# Revit family: НЕВАТОМ_Стакaн монтажный SMK_20240620
name_source: partatom
category: Арматура воздуховодов
units: mm (PartAtom-declared; Revit-internal decimal feet)

## family parameters
Всегда вертикально = Да
На основе рабочей плоскости = Нет
Общий = Нет
При загрузке вырезать с полостями = Нет
Размер круглого соединителя = Использовать диаметр
Тип детали = Присоединяется

## types (12) — shared parameters
ADSK_Единица измерения = шт.
ADSK_Завод-изготовитель = НЕВАТОМ
ADSK_Количество = 1
ADSK_Материал наименование = Оцинкованная сталь
ADSK_Наименование = Стакан монтажный
Nevatom_URL = https://t.me
Ключевая пометка = Вентиляция
Материал = Оцинкованная сталь

## per-type parameters (varying)
| type | A | ADSK_Марка | ADSK_Масса | ADSK_Масса_Текст | ADSK_Размер_Высота | ADSK_Размер_Длина | ADSK_Размер_Ширина | B | D | H | L | L1 | L2 | НЕВАТОМ_Исполнение по комплектующим | НЕВАТОМ_Исполнение по конструкции | НЕВАТОМ_Материал_Нержавеющая сталь | НЕВАТОМ_Материал_Оцинкованная сталь | Сравнение материалов |
| SMK-031 | 400 мм | SMK-031-023-0-0 | 40 | 40.0 кг | 649 мм | 800 мм | 800 мм | 800 мм | 315 мм | 649 мм | 440 мм | 500 мм | 602 мм | 3 мм | 2 мм | Нет | Да | 0 мм |
| SMK-125 | 1435 мм | SMK-125-020-0-0 | 136 | 136.0 кг | 676 мм | 1845 мм | 1845 мм | 1845 мм | 1250 мм | 676 мм | 1550 мм | 1535 мм | 1698 мм | 0 мм | 2 мм | Нет | Да | 0 мм |
| SMK-040 | 470 мм | SMK-040-000-0-0 | 43 | 43.0 кг | 649 мм | 868 мм | 868 мм | 868 мм | 400 мм | 649 мм | 530 мм | 570 мм | 675 мм | 0 мм | 0 мм | Нет | Да | 0 мм |
| SMK-050 | 590 мм | SMK-050-000-0-0 | 53 | 53.0 кг | 649 мм | 1000 мм | 1000 мм | 1000 мм | 500 мм | 649 мм | 630 мм | 690 мм | 795 мм | 0 мм | 0 мм | Нет | Да | 0 мм |
| SMK-063 | 715 мм | SMK-063-000-0-0 | 66 | 66.0 кг | 649 мм | 1125 мм | 1125 мм | 1125 мм | 630 мм | 649 мм | 755 мм | 815 мм | 915 мм | 0 мм | 0 мм | Нет | Да | 0 мм |
| SMK-080 | 921 мм | SMK-080-000-0-0 | 87 | 87.0 кг | 649 мм | 1331 мм | 1331 мм | 1331 мм | 800 мм | 649 мм | 1005 мм | 1021 мм | 1177 мм | 0 мм | 0 мм | Нет | Да | 0 мм |
| SMK-100 | 1205 мм | SMK-100-000-0-0 | 103 | 103.0 кг | 649 мм | 1615 мм | 1615 мм | 1615 мм | 1000 мм | 649 мм | 1280 мм | 1305 мм | 1463 мм | 0 мм | 0 мм | Нет | Да | 0 мм |
| SMK-035 | 400 мм | SMK-035-034-1-0 | 39 | 39.0 кг | 649 мм | 800 мм | 800 мм | 800 мм | 355 мм | 649 мм | 480 мм | 500 мм | 605 мм | 4 мм | 3 мм | Да | Нет | 1 мм |
| SMK-045 | 470 мм | SMK-045-000-0-0 | 42 | 42.0 кг | 649 мм | 868 мм | 868 мм | 868 мм | 450 мм | 649 мм | 580 мм | 570 мм | 675 мм | 0 мм | 0 мм | Нет | Да | 0 мм |
| SMK-071 | 715 мм | SMK-071-000-0-0 | 65 | 65.0 кг | 649 мм | 1125 мм | 1125 мм | 1125 мм | 710 мм | 649 мм | 840 мм | 815 мм | 915 мм | 0 мм | 0 мм | Нет | Да | 0 мм |
| SMK-056 | 590 мм | SMK-056-000-0-0 | 52 | 52.0 кг | 649 мм | 1000 мм | 1000 мм | 1000 мм | 560 мм | 649 мм | 690 мм | 690 мм | 795 мм | 0 мм | 0 мм | Нет | Да | 0 мм |
| SMK-090 | 921 мм | SMK-090-000-0-0 | 87 | 87.0 кг | 649 мм | 1331 мм | 1331 мм | 1331 мм | 900 мм | 649 мм | 1005 мм | 1021 мм | 1177 мм | 0 мм | 0 мм | Нет | Да | 0 мм |
